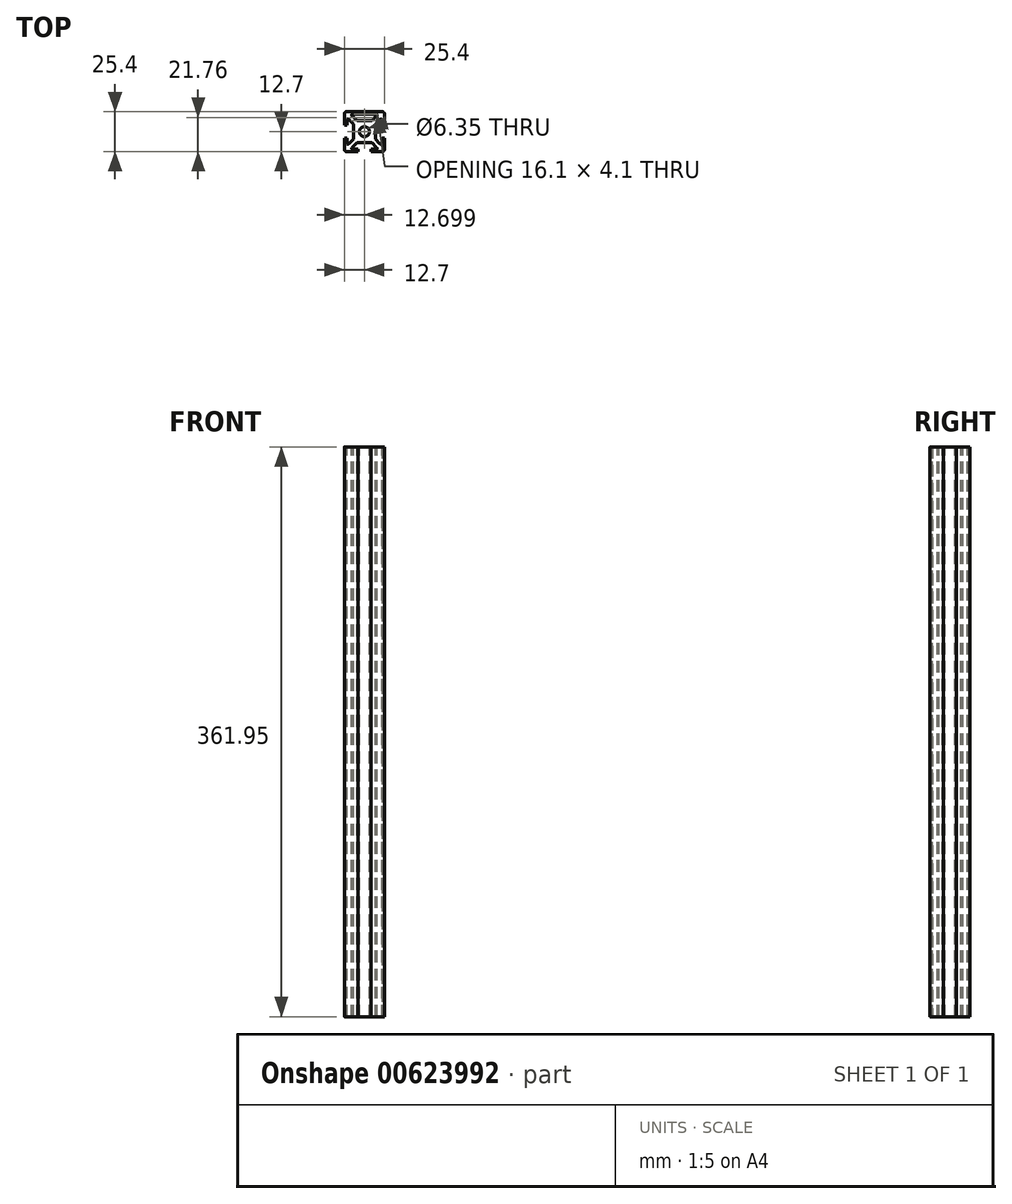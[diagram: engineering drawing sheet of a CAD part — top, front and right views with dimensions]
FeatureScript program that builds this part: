
annotation { "Feature Type Name" : "Feature", "Feature Type Description" : "" }
export const myFeature = defineFeature(function(context is Context, id is Id, definition is map)
    precondition{}
    {
        {
            var Q0;
            Q0=qCreatedBy(makeId("Top.planeOp"),FACE);
            var sketch = newSketch(context, id + "F0", { "sketchPlane" : qUnion([Q0])});
            skLineSegment(sketch, "E0.bottom", {"start": v(12.7, 12.7) * mm, "end": v(-12.7, 12.7) * mm});
            skLineSegment(sketch, "E0.top", {"start": v(12.7, -12.7) * mm, "end": v(-12.7, -12.7) * mm});
            skLineSegment(sketch, "E0.left", {"start": v(12.7, 12.7) * mm, "end": v(12.7, -12.7) * mm});
            skLineSegment(sketch, "E0.right", {"start": v(-12.7, 12.7) * mm, "end": v(-12.7, -12.7) * mm});
            skPoint(sketch, "E0.middle", {"position": v(0, 0) * mm});
            skSolve(sketch);
        }
        {
            var Q0;
            Q0=makeQuery(id+"F0.imprint","IMPRINT",FACE,{"disambiguationData":[TD([[makeQuery(id+"F0.imprint","IMPRINT",EDGE,{"derivedFrom":sQuery(id+"F0.wireOp",EDGE,"E0.bottom")}),1.0]])]});
            extrude(context, id + "F1", {"entities" : qUnion([Q0]), "depth" : 455.93 * mm, "offsetDistance" : 25.4 * mm});
        }
        {
            var Q0;
            Q0=makeQuery(id+"F1.opExtrude","CAP_FACE",FACE,{"disambiguationData":[OSD([sQuery(id+"F0.wireOp",EDGE,"E0.bottom"),sQuery(id+"F0.wireOp",EDGE,"E0.top"),sQuery(id+"F0.wireOp",EDGE,"E0.left"),sQuery(id+"F0.wireOp",EDGE,"E0.right")])],"isStart":false});
            var sketch = newSketch(context, id + "F2", { "sketchPlane" : qUnion([Q0])});
            skLineSegment(sketch, "E1", {"start": v(-7, 4.76) * mm, "end": v(-7, -4.76) * mm});
            skLineSegment(sketch, "E2", {"start": v(-7, -4.76) * mm, "end": v(-11.11, -8.87) * mm});
            skLineSegment(sketch, "E3", {"start": v(-11.11, -8.87) * mm, "end": v(-11.11, -4.1) * mm});
            skLineSegment(sketch, "E4", {"start": v(-11.11, -4.1) * mm, "end": v(-12.7, -4.1) * mm});
            skLineSegment(sketch, "E5", {"start": v(-12.7, -4.1) * mm, "end": v(-12.7, 4.1) * mm});
            skLineSegment(sketch, "E6", {"start": v(-12.7, 4.1) * mm, "end": v(-11.11, 4.1) * mm});
            skLineSegment(sketch, "E7", {"start": v(-11.11, 4.1) * mm, "end": v(-11.11, 8.87) * mm});
            skLineSegment(sketch, "E8", {"start": v(-11.11, 8.87) * mm, "end": v(-7, 4.76) * mm});
            skLineSegment(sketch, "E9", {"start": v(-4.1, -12.7) * mm, "end": v(-4.1, -11.11) * mm});
            skLineSegment(sketch, "E10", {"start": v(-4.1, -11.11) * mm, "end": v(-8.87, -11.11) * mm});
            skLineSegment(sketch, "E11", {"start": v(-8.87, -11.11) * mm, "end": v(-4.76, -7) * mm});
            skLineSegment(sketch, "E12", {"start": v(-4.76, -7) * mm, "end": v(4.76, -7) * mm});
            skLineSegment(sketch, "E13", {"start": v(4.76, -7) * mm, "end": v(8.87, -11.11) * mm});
            skLineSegment(sketch, "E14", {"start": v(8.87, -11.11) * mm, "end": v(4.1, -11.11) * mm});
            skLineSegment(sketch, "E15", {"start": v(4.1, -11.11) * mm, "end": v(4.1, -12.7) * mm});
            skLineSegment(sketch, "E16", {"start": v(4.1, -12.7) * mm, "end": v(-4.1, -12.7) * mm});
            skLineSegment(sketch, "E17", {"start": v(12.7, -4.1) * mm, "end": v(11.11, -4.1) * mm});
            skLineSegment(sketch, "E18", {"start": v(11.11, -4.1) * mm, "end": v(11.11, -8.87) * mm});
            skLineSegment(sketch, "E19", {"start": v(11.11, -8.87) * mm, "end": v(7, -4.76) * mm});
            skLineSegment(sketch, "E20", {"start": v(7, -4.76) * mm, "end": v(7, 4.76) * mm});
            skLineSegment(sketch, "E21", {"start": v(7, 4.76) * mm, "end": v(11.11, 8.87) * mm});
            skLineSegment(sketch, "E22", {"start": v(11.11, 8.87) * mm, "end": v(11.11, 4.1) * mm});
            skLineSegment(sketch, "E23", {"start": v(11.11, 4.1) * mm, "end": v(12.7, 4.1) * mm});
            skLineSegment(sketch, "E24", {"start": v(12.7, 4.1) * mm, "end": v(12.7, -4.1) * mm});
            skLineSegment(sketch, "E25", {"start": v(-4.1, 12.7) * mm, "end": v(-4.1, 11.11) * mm});
            skLineSegment(sketch, "E26", {"start": v(-4.1, 11.11) * mm, "end": v(-8.87, 11.11) * mm});
            skLineSegment(sketch, "E27", {"start": v(-8.87, 11.11) * mm, "end": v(-4.76, 7) * mm});
            skLineSegment(sketch, "E28", {"start": v(-4.76, 7) * mm, "end": v(4.76, 7) * mm});
            skLineSegment(sketch, "E29", {"start": v(4.76, 7) * mm, "end": v(8.87, 11.11) * mm});
            skLineSegment(sketch, "E30", {"start": v(8.87, 11.11) * mm, "end": v(4.1, 11.11) * mm});
            skLineSegment(sketch, "E31", {"start": v(4.1, 11.11) * mm, "end": v(4.1, 12.7) * mm});
            skLineSegment(sketch, "E32", {"start": v(4.1, 12.7) * mm, "end": v(-4.1, 12.7) * mm});
            skSolve(sketch);
        }
        {
            var Q0;
            Q0=makeQuery(id+"F2.imprint","IMPRINT",FACE,{"disambiguationData":[TD([[makeQuery(id+"F2.imprint","IMPRINT",EDGE,{"derivedFrom":sQuery(id+"F2.wireOp",EDGE,"E1")}),-1.0]])]});
            var Q1;
            Q1=makeQuery(id+"F2.imprint","IMPRINT",FACE,{"disambiguationData":[TD([[makeQuery(id+"F2.imprint","IMPRINT",EDGE,{"derivedFrom":sQuery(id+"F2.wireOp",EDGE,"E25")}),1.0]])]});
            var Q2;
            Q2=makeQuery(id+"F2.imprint","IMPRINT",FACE,{"disambiguationData":[TD([[makeQuery(id+"F2.imprint","IMPRINT",EDGE,{"derivedFrom":sQuery(id+"F2.wireOp",EDGE,"E17")}),-1.0]])]});
            var Q3;
            Q3=makeQuery(id+"F2.imprint","IMPRINT",FACE,{"disambiguationData":[TD([[makeQuery(id+"F2.imprint","IMPRINT",EDGE,{"derivedFrom":sQuery(id+"F2.wireOp",EDGE,"E9")}),-1.0]])]});
            extrude(context, id + "F3", {"entities" : qUnion([Q0, Q1, Q2, Q3]), "operationType" : NewBodyOperationType.REMOVE, "oppositeDirection" : true, "depth" : 455.93 * mm, "offsetDistance" : 25.4 * mm});
        }
        {
            var Q0;
            Q0=makeQuery(id+"F1.opExtrude","CAP_FACE",FACE,{"disambiguationData":[OSD([sQuery(id+"F0.wireOp",EDGE,"E0.bottom"),sQuery(id+"F0.wireOp",EDGE,"E0.top"),sQuery(id+"F0.wireOp",EDGE,"E0.left"),sQuery(id+"F0.wireOp",EDGE,"E0.right")])],"isStart":false});
            var sketch = newSketch(context, id + "F4", { "sketchPlane" : qUnion([Q0])});
            skCircle(sketch, "E33", {"center": v(0, 0) * mm, "radius": 3.18 * mm});
            skSolve(sketch);
        }
        {
            var Q0;
            Q0=makeQuery(id+"F4.imprint","IMPRINT",FACE,{"disambiguationData":[TD([[makeQuery(id+"F4.imprint","IMPRINT",EDGE,{"derivedFrom":sQuery(id+"F4.wireOp",EDGE,"E33")}),1.0]])]});
            extrude(context, id + "F5", {"entities" : qUnion([Q0]), "operationType" : NewBodyOperationType.REMOVE, "oppositeDirection" : true, "depth" : 455.93 * mm, "offsetDistance" : 25.4 * mm});
        }
        {
            var Q0;
            Q0=makeQuery(id+"F1.opExtrude","SWEPT_EDGE",EDGE,{"disambiguationData":[OSD([sQuery(id+"F0.wireOp",EDGE,"E0.bottom"),sQuery(id+"F0.wireOp",EDGE,"E0.right")])]});
            var Q1;
            Q1=makeQuery(id+"F1.opExtrude","SWEPT_EDGE",EDGE,{"disambiguationData":[OSD([sQuery(id+"F0.wireOp",EDGE,"E0.bottom"),sQuery(id+"F0.wireOp",EDGE,"E0.left")])]});
            var Q2;
            Q2=makeQuery(id+"F1.opExtrude","SWEPT_EDGE",EDGE,{"disambiguationData":[OSD([sQuery(id+"F0.wireOp",EDGE,"E0.top"),sQuery(id+"F0.wireOp",EDGE,"E0.left")])]});
            var Q3;
            Q3=makeQuery(id+"F1.opExtrude","SWEPT_EDGE",EDGE,{"disambiguationData":[OSD([sQuery(id+"F0.wireOp",EDGE,"E0.top"),sQuery(id+"F0.wireOp",EDGE,"E0.right")])]});
            fillet(context, id + "F6", {"entities" : qUnion([Q0, Q1, Q2, Q3]), "radius" : 1.59 * mm, "tangentPropagation" : true, "rho" : 0.5, "crossSection" : FilletCrossSection.CONIC, "allowEdgeOverflow" : false});
        }
        {
            var Q0;
            Q0=makeQuery(id+"F3.boolean.opBoolean","COPY",EDGE,{"derivedFrom":makeQuery(id+"F3.opExtrude","SWEPT_EDGE",EDGE,{"disambiguationData":[OSD([sQuery(id+"F2.wireOp",EDGE,"E7"),sQuery(id+"F2.wireOp",EDGE,"E8")])]})});
            var Q1;
            Q1=makeQuery(id+"F3.boolean.opBoolean","COPY",EDGE,{"derivedFrom":makeQuery(id+"F3.opExtrude","SWEPT_EDGE",EDGE,{"disambiguationData":[OSD([sQuery(id+"F2.wireOp",EDGE,"E21"),sQuery(id+"F2.wireOp",EDGE,"E22")])]})});
            var Q2;
            Q2=makeQuery(id+"F3.boolean.opBoolean","COPY",EDGE,{"derivedFrom":makeQuery(id+"F3.opExtrude","SWEPT_EDGE",EDGE,{"disambiguationData":[OSD([sQuery(id+"F2.wireOp",EDGE,"E18"),sQuery(id+"F2.wireOp",EDGE,"E19")])]})});
            var Q3;
            Q3=makeQuery(id+"F3.boolean.opBoolean","COPY",EDGE,{"derivedFrom":makeQuery(id+"F3.opExtrude","SWEPT_EDGE",EDGE,{"disambiguationData":[OSD([sQuery(id+"F2.wireOp",EDGE,"E2"),sQuery(id+"F2.wireOp",EDGE,"E3")])]})});
            var Q4;
            Q4=makeQuery(id+"F3.boolean.opBoolean","COPY",EDGE,{"derivedFrom":makeQuery(id+"F3.opExtrude","SWEPT_EDGE",EDGE,{"disambiguationData":[OSD([sQuery(id+"F2.wireOp",EDGE,"E10"),sQuery(id+"F2.wireOp",EDGE,"E11")])]})});
            var Q5;
            Q5=makeQuery(id+"F3.boolean.opBoolean","COPY",EDGE,{"derivedFrom":makeQuery(id+"F3.opExtrude","SWEPT_EDGE",EDGE,{"disambiguationData":[OSD([sQuery(id+"F2.wireOp",EDGE,"E13"),sQuery(id+"F2.wireOp",EDGE,"E14")])]})});
            var Q6;
            Q6=makeQuery(id+"F3.boolean.opBoolean","COPY",EDGE,{"derivedFrom":makeQuery(id+"F3.opExtrude","SWEPT_EDGE",EDGE,{"disambiguationData":[OSD([sQuery(id+"F2.wireOp",EDGE,"E29"),sQuery(id+"F2.wireOp",EDGE,"E30")])]})});
            var Q7;
            Q7=makeQuery(id+"F3.boolean.opBoolean","COPY",EDGE,{"derivedFrom":makeQuery(id+"F3.opExtrude","SWEPT_EDGE",EDGE,{"disambiguationData":[OSD([sQuery(id+"F2.wireOp",EDGE,"E26"),sQuery(id+"F2.wireOp",EDGE,"E27")])]})});
            fillet(context, id + "F7", {"entities" : qUnion([Q0, Q1, Q2, Q3, Q4, Q5, Q6, Q7]), "radius" : 0.8 * mm, "tangentPropagation" : true, "rho" : 0.5, "crossSection" : FilletCrossSection.CONIC, "allowEdgeOverflow" : false});
        }
        {
            var Q0;
            Q0=makeQuery(id+"F1.opExtrude","CAP_FACE",FACE,{"disambiguationData":[OSD([sQuery(id+"F0.wireOp",EDGE,"E0.bottom"),sQuery(id+"F0.wireOp",EDGE,"E0.top"),sQuery(id+"F0.wireOp",EDGE,"E0.left"),sQuery(id+"F0.wireOp",EDGE,"E0.right")])],"isStart":false});
            var sketch = newSketch(context, id + "F8", { "sketchPlane" : qUnion([Q0])});
            skLineSegment(sketch, "E34.bottom", {"start": v(-4.1, 12.7) * mm, "end": v(4.1, 12.7) * mm});
            skLineSegment(sketch, "E34.top", {"start": v(-4.1, 11.11) * mm, "end": v(4.1, 11.11) * mm});
            skLineSegment(sketch, "E34.left", {"start": v(-4.1, 12.7) * mm, "end": v(-4.1, 11.11) * mm});
            skLineSegment(sketch, "E34.right", {"start": v(4.1, 12.7) * mm, "end": v(4.1, 11.11) * mm});
            skSolve(sketch);
        }
        {
            var Q0;
            Q0=makeQuery(id+"F8.imprint","IMPRINT",FACE,{"disambiguationData":[TD([[makeQuery(id+"F8.imprint","IMPRINT",EDGE,{"derivedFrom":sQuery(id+"F8.wireOp",EDGE,"E34.bottom")}),-1.0]])]});
            extrude(context, id + "F9", {"entities" : qUnion([Q0]), "operationType" : NewBodyOperationType.ADD, "oppositeDirection" : true, "depth" : 455.93 * mm, "offsetDistance" : 25.4 * mm});
        }
        {
            var Q0;
            Q0=makeQuery(id+"F9.boolean.opBoolean","MERGE",FACE,{"derivedFrom":[makeQuery(id+"F1.opExtrude","CAP_FACE",FACE,{"disambiguationData":[OSD([sQuery(id+"F0.wireOp",EDGE,"E0.bottom"),sQuery(id+"F0.wireOp",EDGE,"E0.top"),sQuery(id+"F0.wireOp",EDGE,"E0.left"),sQuery(id+"F0.wireOp",EDGE,"E0.right")])],"isStart":false}),makeQuery(id+"F9.opExtrude","CAP_FACE",FACE,{"disambiguationData":[OSD([sQuery(id+"F8.wireOp",EDGE,"E34.bottom"),sQuery(id+"F8.wireOp",EDGE,"E34.top"),sQuery(id+"F8.wireOp",EDGE,"E34.left"),sQuery(id+"F8.wireOp",EDGE,"E34.right")])],"isStart":true})]});
            extrude(context, id + "F10", {"entities" : qUnion([Q0]), "operationType" : NewBodyOperationType.REMOVE, "oppositeDirection" : true, "depth" : 93.98 * mm, "offsetDistance" : 25.4 * mm});
        }
    });
